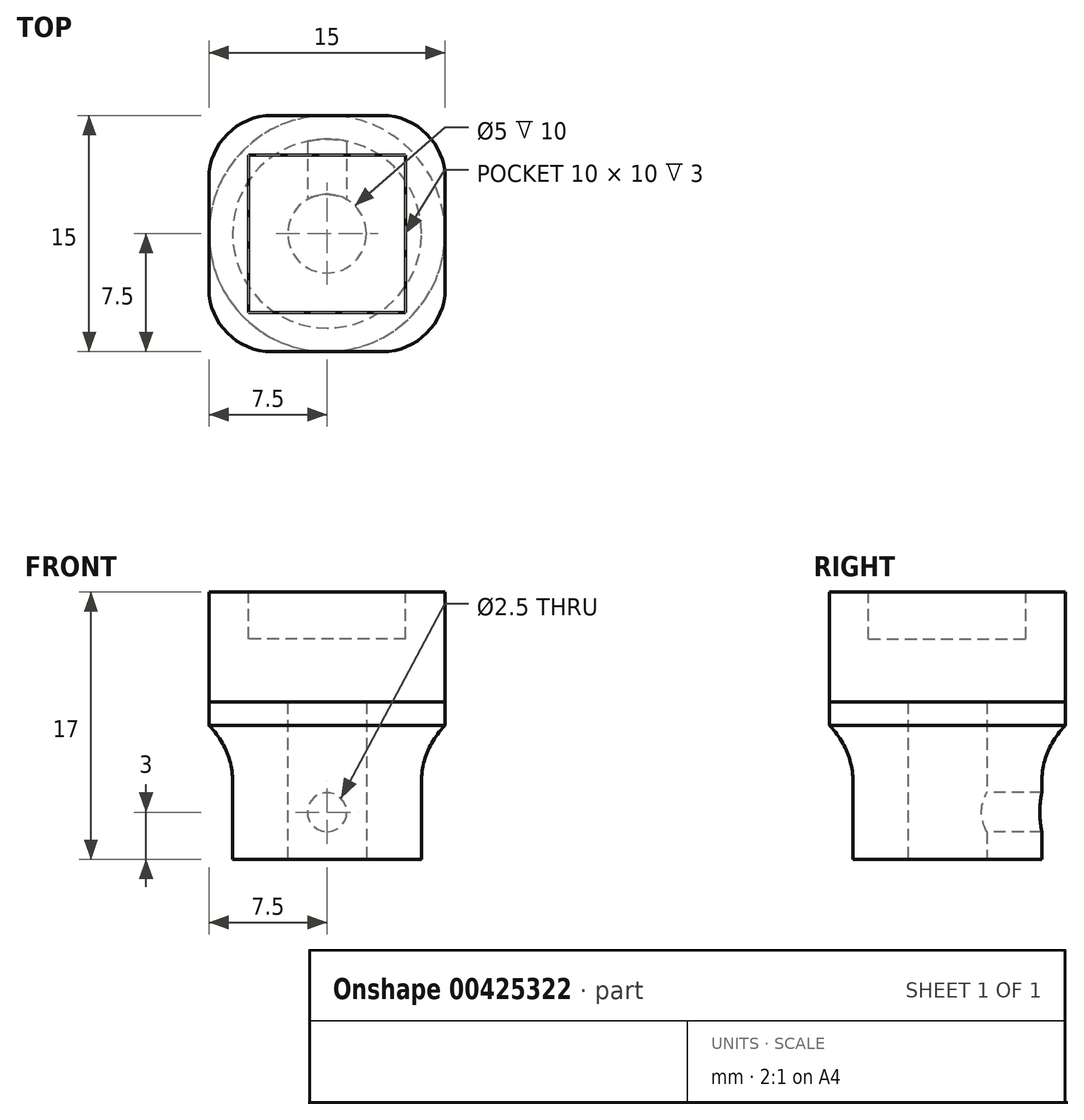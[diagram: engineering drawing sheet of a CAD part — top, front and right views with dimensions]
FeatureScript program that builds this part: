
annotation { "Feature Type Name" : "Feature", "Feature Type Description" : "" }
export const myFeature = defineFeature(function(context is Context, id is Id, definition is map)
    precondition{}
    {
        {
            var Q0;
            Q0=qCreatedBy(makeId("Top.planeOp"),FACE);
            var sketch = newSketch(context, id + "F0", { "sketchPlane" : qUnion([Q0])});
            skCircle(sketch, "E0", {"center": v(0, 0) * mm, "radius": 2.5 * mm});
            skCircle(sketch, "E1", {"center": v(0, 0) * mm, "radius": 6 * mm});
            skSolve(sketch);
        }
        {
            var Q0;
            Q0 = qSketchRegion(id + "F0", true);
            extrude(context, id + "F1", {"entities" : qUnion([Q0]), "depth" : 10 * mm});
        }
        {
            var Q0;
            Q0=makeQuery(id+"F1.opExtrude","CAP_FACE",FACE,{"disambiguationData":[OSD([sQuery(id+"F0.wireOp",EDGE,"E0"),sQuery(id+"F0.wireOp",EDGE,"E1")])],"isStart":false});
            var sketch = newSketch(context, id + "F2", { "sketchPlane" : qUnion([Q0])});
            skLineSegment(sketch, "E2.bottom", {"start": v(7.5, -7.5) * mm, "end": v(-7.5, -7.5) * mm});
            skLineSegment(sketch, "E2.top", {"start": v(7.5, 7.5) * mm, "end": v(-7.5, 7.5) * mm});
            skLineSegment(sketch, "E2.left", {"start": v(7.5, -7.5) * mm, "end": v(7.5, 7.5) * mm});
            skLineSegment(sketch, "E2.right", {"start": v(-7.5, -7.5) * mm, "end": v(-7.5, 7.5) * mm});
            skPoint(sketch, "E2.middle", {"position": v(0, 0) * mm});
            skSolve(sketch);
        }
        {
            var Q0;
            Q0 = qSketchRegion(id + "F2", true);
            extrude(context, id + "F3", {"entities" : qUnion([Q0]), "operationType" : NewBodyOperationType.ADD, "depth" : 7 * mm});
        }
        {
            var Q0;
            Q0=makeQuery(id+"F3.opExtrude","CAP_FACE",FACE,{"disambiguationData":[OSD([sQuery(id+"F2.wireOp",EDGE,"E2.bottom"),sQuery(id+"F2.wireOp",EDGE,"E2.top"),sQuery(id+"F2.wireOp",EDGE,"E2.left"),sQuery(id+"F2.wireOp",EDGE,"E2.right")])],"isStart":false});
            var sketch = newSketch(context, id + "F4", { "sketchPlane" : qUnion([Q0])});
            skLineSegment(sketch, "E3.bottom", {"start": v(5, -5) * mm, "end": v(-5, -5) * mm});
            skLineSegment(sketch, "E3.top", {"start": v(5, 5) * mm, "end": v(-5, 5) * mm});
            skLineSegment(sketch, "E3.left", {"start": v(5, -5) * mm, "end": v(5, 5) * mm});
            skLineSegment(sketch, "E3.right", {"start": v(-5, -5) * mm, "end": v(-5, 5) * mm});
            skPoint(sketch, "E3.middle", {"position": v(0, 0) * mm});
            skSolve(sketch);
        }
        {
            var Q0;
            Q0 = qSketchRegion(id + "F4", true);
            extrude(context, id + "F5", {"entities" : qUnion([Q0]), "operationType" : NewBodyOperationType.REMOVE, "oppositeDirection" : true, "depth" : 3 * mm});
        }
        {
            var Q0;
            Q0=makeQuery(id+"F3.opExtrude","SWEPT_EDGE",EDGE,{"disambiguationData":[OSD([sQuery(id+"F2.wireOp",EDGE,"E2.top"),sQuery(id+"F2.wireOp",EDGE,"E2.left")])]});
            var Q1;
            Q1=makeQuery(id+"F3.opExtrude","SWEPT_EDGE",EDGE,{"disambiguationData":[OSD([sQuery(id+"F2.wireOp",EDGE,"E2.bottom"),sQuery(id+"F2.wireOp",EDGE,"E2.left")])]});
            var Q2;
            Q2=makeQuery(id+"F3.opExtrude","SWEPT_EDGE",EDGE,{"disambiguationData":[OSD([sQuery(id+"F2.wireOp",EDGE,"E2.bottom"),sQuery(id+"F2.wireOp",EDGE,"E2.right")])]});
            var Q3;
            Q3=makeQuery(id+"F3.opExtrude","SWEPT_EDGE",EDGE,{"disambiguationData":[OSD([sQuery(id+"F2.wireOp",EDGE,"E2.top"),sQuery(id+"F2.wireOp",EDGE,"E2.right")])]});
            fillet(context, id + "F6", {"entities" : qUnion([Q0, Q1, Q2, Q3]), "radius" : 4 * mm, "tangentPropagation" : true, "allowEdgeOverflow" : false});
        }
        {
            var Q0;
            {var subQ0=sQuery(id+"F2.wireOp",EDGE,"E2.left");var subQ1=sQuery(id+"F2.wireOp",EDGE,"E2.top");var subQ2=sQuery(id+"F2.wireOp",EDGE,"E2.bottom");var subQ3=sQuery(id+"F2.wireOp",EDGE,"E2.right");Q0=makeQuery(id+"F3.boolean.opBoolean","SPLIT",FACE,{"disambiguationData":[TD([makeQuery(id+"F1.opExtrude","SWEPT_FACE",FACE,{"disambiguationData":[OSD([sQuery(id+"F0.wireOp",EDGE,"E1")])]})])],"derivedFrom":makeQuery(id+"F3.opExtrude","CAP_FACE",FACE,{"disambiguationData":[OSD([subQ2,subQ1,subQ0,subQ3])],"isStart":true})});}
            var sketch = newSketch(context, id + "F7", { "sketchPlane" : qUnion([Q0])});
            skCircle(sketch, "E4", {"center": v(0, 0) * mm, "radius": 6 * mm});
            skCircle(sketch, "E5", {"center": v(0, 0) * mm, "radius": 7.5 * mm});
            skSolve(sketch);
        }
        {
            var Q0;
            Q0 = qSketchRegion(id + "F7", true);
            extrude(context, id + "F8", {"entities" : qUnion([Q0]), "operationType" : NewBodyOperationType.ADD, "depth" : 3 * mm});
        }
        {
            var Q0;
            Q0=makeQuery(id+"F8.opExtrude","CAP_EDGE",EDGE,{"disambiguationData":[OSD([sQuery(id+"F7.wireOp",EDGE,"E5")])],"isStart":false});
            chamfer(context, id + "F9", {"entities" : qUnion([Q0]), "width" : 1.5 * mm, "tangentPropagation" : true});
        }
        {
            var Q0;
            Q0=makeQuery(id+"F8.opExtrude","CAP_EDGE",EDGE,{"disambiguationData":[OSD([sQuery(id+"F7.wireOp",EDGE,"E4")])],"isStart":false});
            var Q1;
            Q1=makeQuery(id+"F9.opChamfer","BLEND_EDGE",EDGE,{"blendedFrom":[makeQuery(id+"F8.opExtrude","CAP_EDGE",EDGE,{"disambiguationData":[OSD([sQuery(id+"F7.wireOp",EDGE,"E5")])],"isStart":false}),makeQuery(id+"F1.opExtrude","SWEPT_FACE",FACE,{"disambiguationData":[OSD([sQuery(id+"F0.wireOp",EDGE,"E1")])]})],"blendedInto":[makeQuery(id+"F1.opExtrude","SWEPT_FACE",FACE,{"disambiguationData":[OSD([sQuery(id+"F0.wireOp",EDGE,"E1")])]})]});
            fillet(context, id + "F10", {"entities" : qUnion([Q0, Q1]), "radius" : 5 * mm, "tangentPropagation" : true, "allowEdgeOverflow" : false});
        }
        {
            var Q0;
            Q0=qCreatedBy(makeId("Front.planeOp"),FACE);
            var sketch = newSketch(context, id + "F11", { "sketchPlane" : qUnion([Q0])});
            skCircle(sketch, "E6", {"center": v(0, 3) * mm, "radius": 1.25 * mm});
            skSolve(sketch);
        }
        {
            var Q0;
            Q0 = qSketchRegion(id + "F11", true);
            extrude(context, id + "F12", {"entities" : qUnion([Q0]), "operationType" : NewBodyOperationType.REMOVE, "oppositeDirection" : true, "depth" : 10 * mm});
        }
    });
